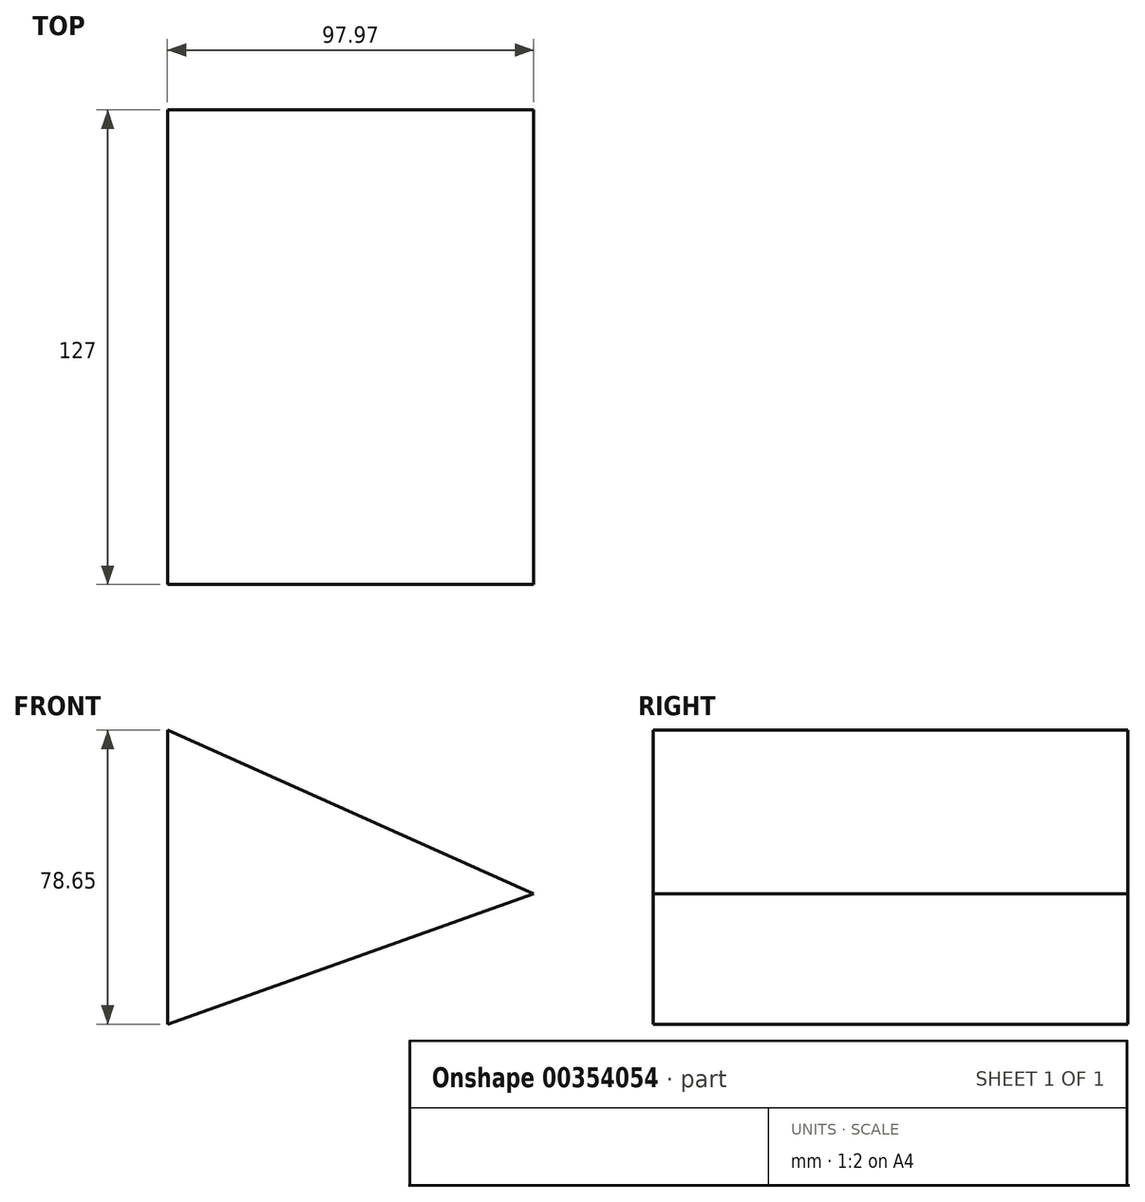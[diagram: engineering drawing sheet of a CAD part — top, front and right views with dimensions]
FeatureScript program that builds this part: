
annotation { "Feature Type Name" : "Feature", "Feature Type Description" : "" }
export const myFeature = defineFeature(function(context is Context, id is Id, definition is map)
    precondition{}
    {
        {
            var Q0;
            Q0=qCreatedBy(makeId("Front.planeOp"),FACE);
            var sketch = newSketch(context, id + "F0", { "sketchPlane" : qUnion([Q0])});
            skLineSegment(sketch, "E0", {"start": v(-49.26, 43.82) * mm, "end": v(-49.26, -34.83) * mm});
            skLineSegment(sketch, "E1", {"start": v(-49.26, -34.83) * mm, "end": v(48.71, 0) * mm});
            skLineSegment(sketch, "E2", {"start": v(48.71, 0) * mm, "end": v(-49.26, 43.82) * mm});
            skSolve(sketch);
        }
        {
            var Q0;
            Q0=makeQuery(id+"F0.imprint","IMPRINT",FACE,{"disambiguationData":[TD([[makeQuery(id+"F0.imprint","IMPRINT",EDGE,{"derivedFrom":sQuery(id+"F0.wireOp",EDGE,"E0")}),1.0]])]});
            extrude(context, id + "F1", {"entities" : qUnion([Q0]), "depth" : 127 * mm});
        }
    });
